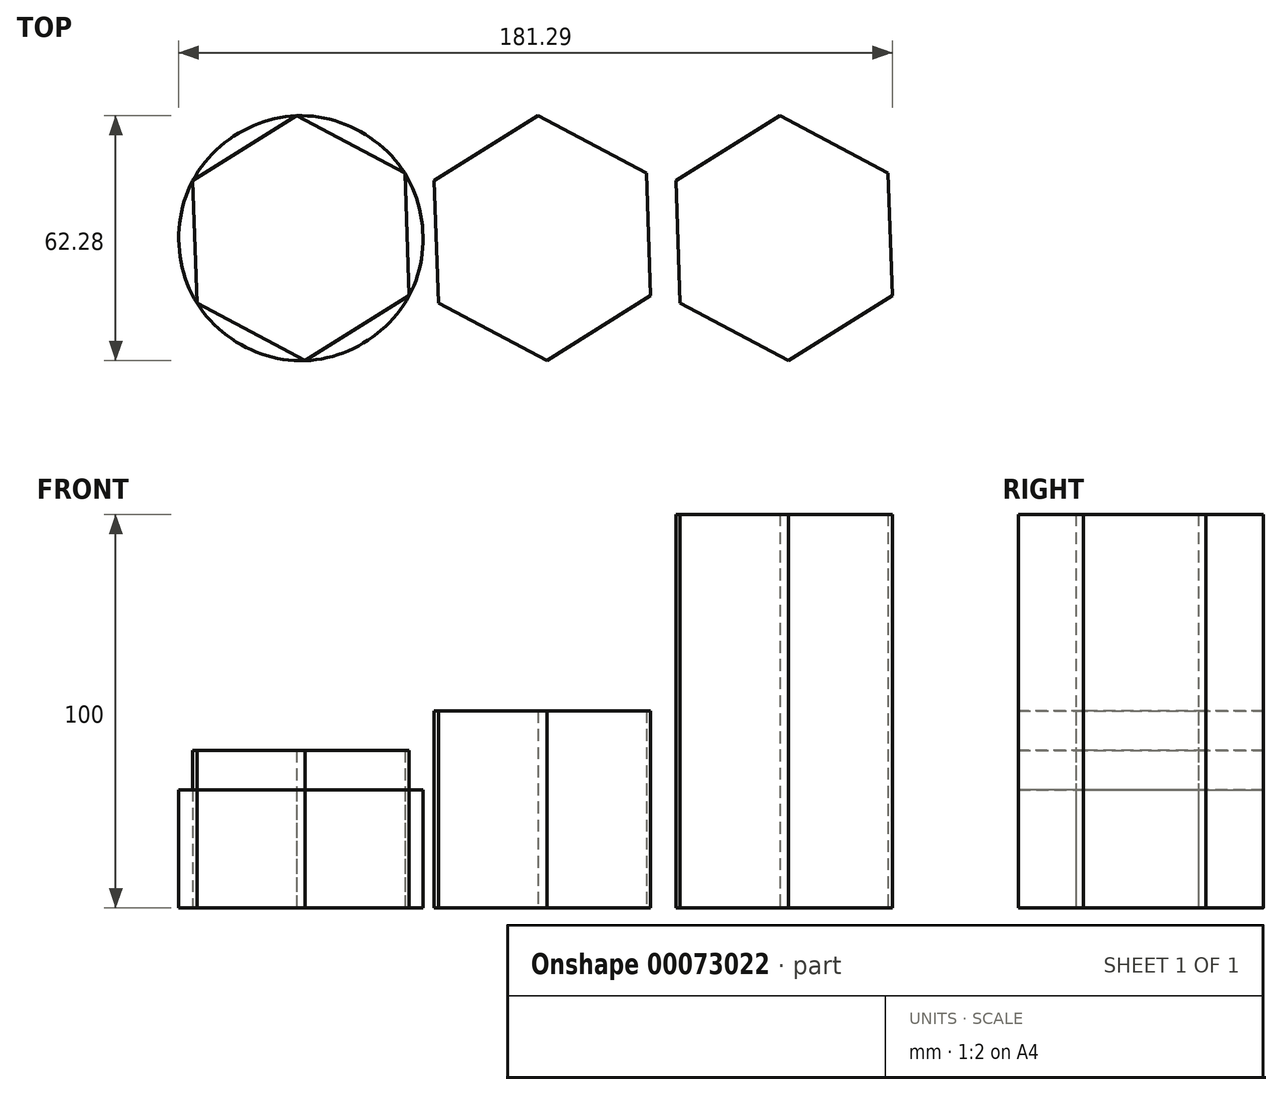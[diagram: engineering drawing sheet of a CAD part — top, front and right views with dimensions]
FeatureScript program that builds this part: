
annotation { "Feature Type Name" : "Feature", "Feature Type Description" : "" }
export const myFeature = defineFeature(function(context is Context, id is Id, definition is map)
    precondition{}
    {
        {
            var Q0;
            Q0=qCreatedBy(makeId("Top.planeOp"),FACE);
            var sketch = newSketch(context, id + "F0", { "sketchPlane" : qUnion([Q0])});
            skCircle(sketch, "E0.cCircle", {"center": v(-26.25, 22.87) * mm, "radius": 26.97 * mm, "construction": true});
            skLineSegment(sketch, "E0.0", {"start": v(1.25, 8.25) * mm, "end": v(-25.16, -8.25) * mm});
            skLineSegment(sketch, "E0.1", {"start": v(-25.16, -8.25) * mm, "end": v(-52.66, 6.37) * mm});
            skLineSegment(sketch, "E0.2", {"start": v(-52.66, 6.37) * mm, "end": v(-53.75, 37.49) * mm});
            skLineSegment(sketch, "E0.3", {"start": v(-53.75, 37.49) * mm, "end": v(-27.34, 54) * mm});
            skLineSegment(sketch, "E0.4", {"start": v(-27.34, 54) * mm, "end": v(0.16, 39.38) * mm});
            skLineSegment(sketch, "E0.5", {"start": v(0.16, 39.38) * mm, "end": v(1.25, 8.25) * mm});
            skPoint(sketch, "E0.0.midPoint", {"position": v(-11.96, 0) * mm});
            skFitSpline(sketch, "E1", {"points": [v(-25.16, -8.25) * mm, v(1.25, 8.25) * mm, v(0.16, 39.38) * mm, v(-27.34, 54) * mm, v(-53.75, 37.49) * mm, v(-52.66, 6.37) * mm, v(-25.16, -8.25) * mm]});
            skCircle(sketch, "E2.1.0.0", {"center": v(35.14, 22.87) * mm, "radius": 26.97 * mm, "construction": true});
            skLineSegment(sketch, "E2.1.0.1", {"start": v(34.05, 54) * mm, "end": v(61.55, 39.38) * mm});
            skLineSegment(sketch, "E2.1.0.2", {"start": v(7.64, 37.49) * mm, "end": v(34.05, 54) * mm});
            skLineSegment(sketch, "E2.1.0.3", {"start": v(8.73, 6.37) * mm, "end": v(7.64, 37.49) * mm});
            skLineSegment(sketch, "E2.1.0.4", {"start": v(36.23, -8.25) * mm, "end": v(8.73, 6.37) * mm});
            skLineSegment(sketch, "E2.1.0.5", {"start": v(62.64, 8.25) * mm, "end": v(36.23, -8.25) * mm});
            skLineSegment(sketch, "E2.1.0.6", {"start": v(61.55, 39.38) * mm, "end": v(62.64, 8.25) * mm});
            skCircle(sketch, "E2.2.0.0", {"center": v(96.52, 22.87) * mm, "radius": 26.97 * mm, "construction": true});
            skLineSegment(sketch, "E2.2.0.1", {"start": v(95.43, 54) * mm, "end": v(122.93, 39.38) * mm});
            skLineSegment(sketch, "E2.2.0.2", {"start": v(69.02, 37.49) * mm, "end": v(95.43, 54) * mm});
            skLineSegment(sketch, "E2.2.0.3", {"start": v(70.11, 6.37) * mm, "end": v(69.02, 37.49) * mm});
            skLineSegment(sketch, "E2.2.0.4", {"start": v(97.61, -8.25) * mm, "end": v(70.11, 6.37) * mm});
            skLineSegment(sketch, "E2.2.0.5", {"start": v(124.02, 8.25) * mm, "end": v(97.61, -8.25) * mm});
            skLineSegment(sketch, "E2.2.0.6", {"start": v(122.93, 39.38) * mm, "end": v(124.02, 8.25) * mm});
            skLineSegment(sketch, "E2.direction1", {"start": v(-26.25, 22.87) * mm, "end": v(35.14, 22.87) * mm, "construction": true});
            skSolve(sketch);
        }
        {
            var Q0;
            {var subQ0=sQuery(id+"F0.wireOp",EDGE,"E0.2");Q0=makeQuery(id+"F0.imprint","IMPRINT",FACE,{"disambiguationData":[TD([[makeQuery(id+"F0.imprint","IMPRINT",EDGE,{"derivedFrom":subQ0}),1.0]])]});}
            var Q1;
            {var subQ0=sQuery(id+"F0.wireOp",EDGE,"E0.3");Q1=makeQuery(id+"F0.imprint","IMPRINT",FACE,{"disambiguationData":[TD([[makeQuery(id+"F0.imprint","IMPRINT",EDGE,{"derivedFrom":subQ0}),1.0]])]});}
            var Q2;
            {var subQ0=sQuery(id+"F0.wireOp",EDGE,"E0.4");Q2=makeQuery(id+"F0.imprint","IMPRINT",FACE,{"disambiguationData":[TD([[makeQuery(id+"F0.imprint","IMPRINT",EDGE,{"derivedFrom":subQ0}),1.0]])]});}
            var Q3;
            {var subQ0=sQuery(id+"F0.wireOp",EDGE,"E0.5");Q3=makeQuery(id+"F0.imprint","IMPRINT",FACE,{"disambiguationData":[TD([[makeQuery(id+"F0.imprint","IMPRINT",EDGE,{"derivedFrom":subQ0}),1.0]])]});}
            var Q4;
            {var subQ0=sQuery(id+"F0.wireOp",EDGE,"E0.0");Q4=makeQuery(id+"F0.imprint","IMPRINT",FACE,{"disambiguationData":[TD([[makeQuery(id+"F0.imprint","IMPRINT",EDGE,{"derivedFrom":subQ0}),1.0]])]});}
            var Q5;
            {var subQ0=sQuery(id+"F0.wireOp",EDGE,"E0.1");Q5=makeQuery(id+"F0.imprint","IMPRINT",FACE,{"disambiguationData":[TD([[makeQuery(id+"F0.imprint","IMPRINT",EDGE,{"derivedFrom":subQ0}),1.0]])]});}
            extrude(context, id + "F1", {"entities" : qUnion([Q0, Q1, Q2, Q3, Q4, Q5]), "depth" : 30 * mm});
        }
        {
            var Q0;
            Q0=makeQuery(id+"F0.imprint","IMPRINT",FACE,{"disambiguationData":[TD([[makeQuery(id+"F0.imprint","IMPRINT",EDGE,{"derivedFrom":sQuery(id+"F0.wireOp",EDGE,"E0.0")}),-1.0]])]});
            extrude(context, id + "F2", {"entities" : qUnion([Q0]), "depth" : 40 * mm});
        }
        {
            var Q0;
            Q0=makeQuery(id+"F0.imprint","IMPRINT",FACE,{"disambiguationData":[TD([[makeQuery(id+"F0.imprint","IMPRINT",EDGE,{"derivedFrom":sQuery(id+"F0.wireOp",EDGE,"E2.1.0.1")}),-1.0]])]});
            extrude(context, id + "F3", {"entities" : qUnion([Q0]), "depth" : 50 * mm});
        }
        {
            var Q0;
            Q0=makeQuery(id+"F0.imprint","IMPRINT",FACE,{"disambiguationData":[TD([[makeQuery(id+"F0.imprint","IMPRINT",EDGE,{"derivedFrom":sQuery(id+"F0.wireOp",EDGE,"E2.2.0.1")}),-1.0]])]});
            extrude(context, id + "F4", {"entities" : qUnion([Q0]), "depth" : 100 * mm});
        }
    });
